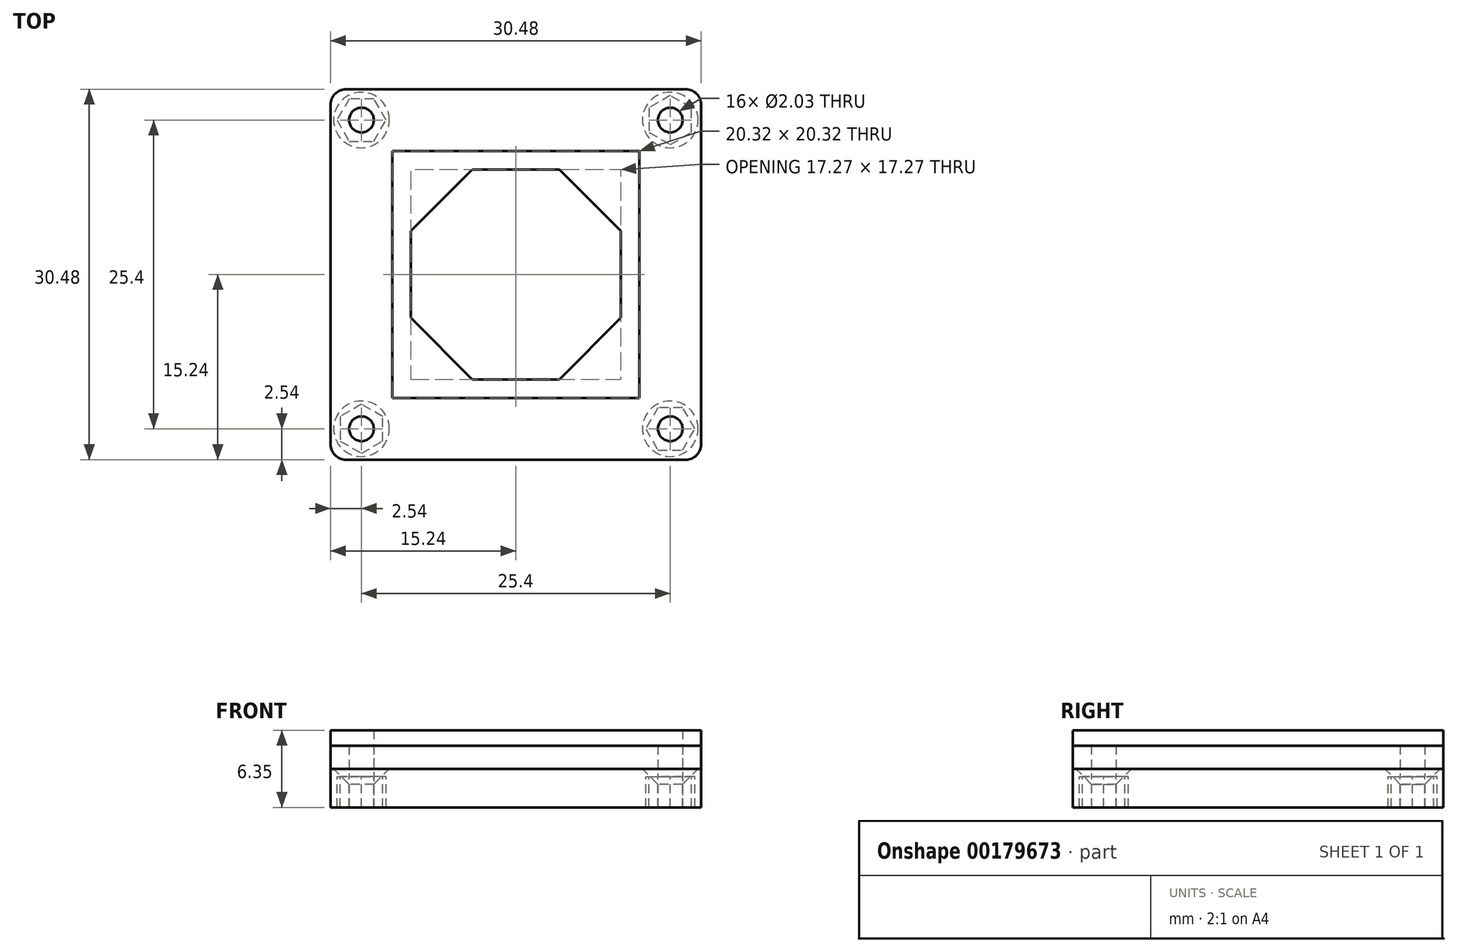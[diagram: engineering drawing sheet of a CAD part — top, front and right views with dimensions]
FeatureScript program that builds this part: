
annotation { "Feature Type Name" : "Feature", "Feature Type Description" : "" }
export const myFeature = defineFeature(function(context is Context, id is Id, definition is map)
    precondition{}
    {
        {
            var Q0;
            Q0=qCreatedBy(makeId("Front.planeOp"),FACE);
            var sketch = newSketch(context, id + "F0", { "sketchPlane" : qUnion([Q0])});
            skLineSegment(sketch, "E0", {"start": v(0, 11.24) * mm, "end": v(0, -12.26) * mm, "construction": true});
            skSolve(sketch);
        }
        {
            var Q0;
            Q0=qCreatedBy(makeId("Top.planeOp"),FACE);
            var sketch = newSketch(context, id + "F1", { "sketchPlane" : qUnion([Q0])});
            skLineSegment(sketch, "E1.bottom", {"start": v(10.16, 10.16) * mm, "end": v(-10.16, 10.16) * mm});
            skLineSegment(sketch, "E1.top", {"start": v(10.16, -10.16) * mm, "end": v(-10.16, -10.16) * mm});
            skLineSegment(sketch, "E1.left", {"start": v(10.16, 10.16) * mm, "end": v(10.16, -10.16) * mm});
            skLineSegment(sketch, "E1.right", {"start": v(-10.16, 10.16) * mm, "end": v(-10.16, -10.16) * mm});
            skPoint(sketch, "E1.middle", {"position": v(0, 0) * mm});
            skCircle(sketch, "E2.cCircle", {"center": v(0, 0) * mm, "radius": 8.64 * mm, "construction": true});
            skPoint(sketch, "E2.cCircle.perimeterSnap0", {"position": v(-10.16, 0) * mm});
            skLineSegment(sketch, "E2.0", {"start": v(-8.64, -3.58) * mm, "end": v(-8.64, 3.58) * mm});
            skLineSegment(sketch, "E2.1", {"start": v(-8.64, 3.58) * mm, "end": v(-3.58, 8.64) * mm});
            skLineSegment(sketch, "E2.2", {"start": v(-3.58, 8.64) * mm, "end": v(3.58, 8.64) * mm});
            skLineSegment(sketch, "E2.3", {"start": v(3.58, 8.64) * mm, "end": v(8.64, 3.58) * mm});
            skLineSegment(sketch, "E2.4", {"start": v(8.64, 3.58) * mm, "end": v(8.64, -3.58) * mm});
            skLineSegment(sketch, "E2.5", {"start": v(8.64, -3.58) * mm, "end": v(3.58, -8.64) * mm});
            skLineSegment(sketch, "E2.6", {"start": v(3.58, -8.64) * mm, "end": v(-3.58, -8.64) * mm});
            skLineSegment(sketch, "E2.7", {"start": v(-3.58, -8.64) * mm, "end": v(-8.64, -3.58) * mm});
            skPoint(sketch, "E2.0.midPoint", {"position": v(-8.64, 0) * mm});
            skPoint(sketch, "E2.0.midPoint.positionSnap0", {"position": v(-10.16, 0) * mm});
            skLineSegment(sketch, "E3.0", {"start": v(-15.24, 15.24) * mm, "end": v(-15.24, -15.24) * mm});
            skLineSegment(sketch, "E3.1", {"start": v(15.24, 15.24) * mm, "end": v(-15.24, 15.24) * mm});
            skLineSegment(sketch, "E3.2", {"start": v(15.24, 15.24) * mm, "end": v(15.24, -15.24) * mm});
            skLineSegment(sketch, "E3.3", {"start": v(15.24, -15.24) * mm, "end": v(-15.24, -15.24) * mm});
            skLineSegment(sketch, "E4", {"start": v(10.16, -10.16) * mm, "end": v(15.24, -15.24) * mm});
            skPoint(sketch, "E5", {"position": v(12.7, -12.7) * mm});
            skCircle(sketch, "E6", {"center": v(12.7, -12.7) * mm, "radius": 1.02 * mm});
            skCircle(sketch, "E7.1.0", {"center": v(12.7, 12.7) * mm, "radius": 1.02 * mm});
            skCircle(sketch, "E7.2.0", {"center": v(-12.7, 12.7) * mm, "radius": 1.02 * mm});
            skCircle(sketch, "E7.3.0", {"center": v(-12.7, -12.7) * mm, "radius": 1.02 * mm});
            skSolve(sketch);
        }
        {
            var Q0;
            Q0=makeQuery(id+"F1.imprint","IMPRINT",FACE,{"disambiguationData":[TD([[makeQuery(id+"F1.imprint","IMPRINT",EDGE,{"derivedFrom":sQuery(id+"F1.wireOp",EDGE,"E1.bottom")}),1.0]])]});
            var Q1;
            Q1=makeQuery(id+"F1.imprint","IMPRINT",FACE,{"disambiguationData":[TD([[makeQuery(id+"F1.imprint","IMPRINT",EDGE,{"derivedFrom":sQuery(id+"F1.wireOp",EDGE,"E1.bottom")}),-1.0]])]});
            extrude(context, id + "F2", {"entities" : qUnion([Q0, Q1]), "depth" : 6.35 * mm});
        }
        {
            var Q0;
            Q0=makeQuery(id+"F2.opExtrude","SWEPT_EDGE",EDGE,{"disambiguationData":[OSD([sQuery(id+"F1.wireOp",EDGE,"E3.0"),sQuery(id+"F1.wireOp",EDGE,"E3.1")])]});
            var Q1;
            Q1=makeQuery(id+"F2.opExtrude","SWEPT_EDGE",EDGE,{"disambiguationData":[OSD([sQuery(id+"F1.wireOp",EDGE,"E3.0"),sQuery(id+"F1.wireOp",EDGE,"E3.3")])]});
            var Q2;
            Q2=makeQuery(id+"F2.opExtrude","SWEPT_EDGE",EDGE,{"disambiguationData":[OSD([sQuery(id+"F1.wireOp",EDGE,"E3.1"),sQuery(id+"F1.wireOp",EDGE,"E3.2")])]});
            var Q3;
            Q3=makeQuery(id+"F2.opExtrude","SWEPT_EDGE",EDGE,{"disambiguationData":[OSD([sQuery(id+"F1.wireOp",EDGE,"E3.2"),sQuery(id+"F1.wireOp",EDGE,"E3.3")])]});
            fillet(context, id + "F3", {"entities" : qUnion([Q0, Q1, Q2, Q3]), "radius" : 1.27 * mm, "tangentPropagation" : true, "allowEdgeOverflow" : false});
        }
        {
            var Q0;
            Q0=makeQuery(id+"F1.imprint","IMPRINT",FACE,{"disambiguationData":[TD([[makeQuery(id+"F1.imprint","IMPRINT",EDGE,{"derivedFrom":sQuery(id+"F1.wireOp",EDGE,"E1.bottom")}),-1.0]])]});
            extrude(context, id + "F4", {"entities" : qUnion([Q0]), "depth" : 6.35 * mm});
        }
        {
            var Q0;
            Q0=makeQuery(id+"F4.opExtrude","SWEPT_EDGE",EDGE,{"disambiguationData":[OSD([sQuery(id+"F1.wireOp",EDGE,"E3.1"),sQuery(id+"F1.wireOp",EDGE,"E3.2")])]});
            var Q1;
            Q1=makeQuery(id+"F4.opExtrude","SWEPT_EDGE",EDGE,{"disambiguationData":[OSD([sQuery(id+"F1.wireOp",EDGE,"E3.2"),sQuery(id+"F1.wireOp",EDGE,"E3.3")])]});
            var Q2;
            Q2=makeQuery(id+"F4.opExtrude","SWEPT_EDGE",EDGE,{"disambiguationData":[OSD([sQuery(id+"F1.wireOp",EDGE,"E3.0"),sQuery(id+"F1.wireOp",EDGE,"E3.1")])]});
            var Q3;
            Q3=makeQuery(id+"F4.opExtrude","SWEPT_EDGE",EDGE,{"disambiguationData":[OSD([sQuery(id+"F1.wireOp",EDGE,"E3.0"),sQuery(id+"F1.wireOp",EDGE,"E3.3")])]});
            fillet(context, id + "F5", {"entities" : qUnion([Q0, Q1, Q2, Q3]), "radius" : 1.27 * mm, "tangentPropagation" : true, "allowEdgeOverflow" : false});
        }
        {
            var Q0;
            Q0=makeQuery(id+"F1.imprint","IMPRINT",FACE,{"disambiguationData":[TD([[makeQuery(id+"F1.imprint","IMPRINT",EDGE,{"derivedFrom":sQuery(id+"F1.wireOp",EDGE,"E1.bottom")}),-1.0]])]});
            var Q1;
            Q1=makeQuery(id+"F1.imprint","IMPRINT",FACE,{"disambiguationData":[TD([[makeQuery(id+"F1.imprint","IMPRINT",EDGE,{"derivedFrom":sQuery(id+"F1.wireOp",EDGE,"E1.bottom")}),1.0]])]});
            var Q2;
            Q2=makeQuery(id+"F1.imprint","IMPRINT",FACE,{"disambiguationData":[TD([[makeQuery(id+"F1.imprint","IMPRINT",EDGE,{"derivedFrom":sQuery(id+"F1.wireOp",EDGE,"E2.0")}),-1.0]])]});
            extrude(context, id + "F6", {"entities" : qUnion([Q0, Q1, Q2]), "depth" : 3.17 * mm});
        }
        {
            var Q0;
            Q0=makeQuery(id+"F6.opExtrude","SWEPT_EDGE",EDGE,{"disambiguationData":[OSD([sQuery(id+"F1.wireOp",EDGE,"E3.0"),sQuery(id+"F1.wireOp",EDGE,"E3.1")])]});
            var Q1;
            Q1=makeQuery(id+"F6.opExtrude","SWEPT_EDGE",EDGE,{"disambiguationData":[OSD([sQuery(id+"F1.wireOp",EDGE,"E3.1"),sQuery(id+"F1.wireOp",EDGE,"E3.2")])]});
            var Q2;
            Q2=makeQuery(id+"F6.opExtrude","SWEPT_EDGE",EDGE,{"disambiguationData":[OSD([sQuery(id+"F1.wireOp",EDGE,"E3.2"),sQuery(id+"F1.wireOp",EDGE,"E3.3")])]});
            var Q3;
            Q3=makeQuery(id+"F6.opExtrude","SWEPT_EDGE",EDGE,{"disambiguationData":[OSD([sQuery(id+"F1.wireOp",EDGE,"E3.0"),sQuery(id+"F1.wireOp",EDGE,"E3.3")])]});
            fillet(context, id + "F7", {"entities" : qUnion([Q0, Q1, Q2, Q3]), "radius" : 1.27 * mm, "tangentPropagation" : true, "allowEdgeOverflow" : false});
        }
        {
            var Q0;
            Q0=makeQuery(id+"F1.imprint","IMPRINT",FACE,{"disambiguationData":[TD([[makeQuery(id+"F1.imprint","IMPRINT",EDGE,{"derivedFrom":sQuery(id+"F1.wireOp",EDGE,"E1.bottom")}),-1.0]])]});
            var Q1;
            Q1=makeQuery(id+"F1.imprint","IMPRINT",FACE,{"disambiguationData":[TD([[makeQuery(id+"F1.imprint","IMPRINT",EDGE,{"derivedFrom":sQuery(id+"F1.wireOp",EDGE,"E1.bottom")}),1.0]])]});
            var Q2;
            Q2=makeQuery(id+"F1.imprint","IMPRINT",FACE,{"disambiguationData":[TD([[makeQuery(id+"F1.imprint","IMPRINT",EDGE,{"derivedFrom":sQuery(id+"F1.wireOp",EDGE,"E2.0")}),-1.0]])]});
            extrude(context, id + "F8", {"entities" : qUnion([Q0, Q1, Q2]), "depth" : 5.08 * mm});
        }
        {
            var Q0;
            Q0=makeQuery(id+"F8.opExtrude","CAP_FACE",FACE,{"disambiguationData":[OSD([sQuery(id+"F1.wireOp",EDGE,"E3.0"),sQuery(id+"F1.wireOp",EDGE,"E3.1"),sQuery(id+"F1.wireOp",EDGE,"E3.2"),sQuery(id+"F1.wireOp",EDGE,"E3.3"),sQuery(id+"F1.wireOp",EDGE,"E6"),sQuery(id+"F1.wireOp",EDGE,"E7.1.0"),sQuery(id+"F1.wireOp",EDGE,"E7.2.0"),sQuery(id+"F1.wireOp",EDGE,"E7.3.0")])],"isStart":true});
            var sketch = newSketch(context, id + "F9", { "sketchPlane" : qUnion([Q0])});
            skCircle(sketch, "E8.cCircle", {"center": v(-12.7, 12.7) * mm, "radius": 1.75 * mm, "construction": true});
            skLineSegment(sketch, "E8.0", {"start": v(-14.45, 11.7) * mm, "end": v(-14.45, 13.7) * mm});
            skLineSegment(sketch, "E8.1", {"start": v(-14.45, 13.7) * mm, "end": v(-12.7, 14.72) * mm});
            skLineSegment(sketch, "E8.2", {"start": v(-12.7, 14.72) * mm, "end": v(-10.95, 13.7) * mm});
            skLineSegment(sketch, "E8.3", {"start": v(-10.95, 13.7) * mm, "end": v(-10.95, 11.7) * mm});
            skLineSegment(sketch, "E8.4", {"start": v(-10.95, 11.7) * mm, "end": v(-12.7, 10.68) * mm});
            skLineSegment(sketch, "E8.5", {"start": v(-12.7, 10.68) * mm, "end": v(-14.45, 11.7) * mm});
            skPoint(sketch, "E8.0.midPoint", {"position": v(-14.45, 12.7) * mm});
            skSolve(sketch);
        }
        {
            var Q0;
            Q0=makeQuery(id+"F9.imprint","IMPRINT",FACE,{"disambiguationData":[TD([[makeQuery(id+"F9.imprint","IMPRINT",EDGE,{"derivedFrom":sQuery(id+"F9.wireOp",EDGE,"E8.0")}),-1.0]])]});
            extrude(context, id + "F10", {"entities" : qUnion([Q0]), "depth" : 5.08 * mm, "symmetric" : true});
        }
        {
            var Q0;
            Q0=makeQuery(id+"F10.opExtrude","SWEPT_BODY",BODY,{"disambiguationData":[OSD([sQuery(id+"F1.wireOp",EDGE,"E7.3.0"),sQuery(id+"F9.wireOp",EDGE,"E8.0"),sQuery(id+"F9.wireOp",EDGE,"E8.1"),sQuery(id+"F9.wireOp",EDGE,"E8.2"),sQuery(id+"F9.wireOp",EDGE,"E8.3"),sQuery(id+"F9.wireOp",EDGE,"E8.4"),sQuery(id+"F9.wireOp",EDGE,"E8.5")])]});
            var Q1;
            Q1=sQuery(id+"F0.wireOp",EDGE,"E0");
            circularPattern(context, id + "F11", {"entities" : qUnion([Q0]), "axis" : qUnion([Q1]), "angle" : 270 * degree, "instanceCount" : 4});
        }
        {
            var Q0;
            Q0=makeQuery(id+"F10.opExtrude","SWEPT_BODY",BODY,{"disambiguationData":[OSD([sQuery(id+"F1.wireOp",EDGE,"E7.3.0"),sQuery(id+"F9.wireOp",EDGE,"E8.0"),sQuery(id+"F9.wireOp",EDGE,"E8.1"),sQuery(id+"F9.wireOp",EDGE,"E8.2"),sQuery(id+"F9.wireOp",EDGE,"E8.3"),sQuery(id+"F9.wireOp",EDGE,"E8.4"),sQuery(id+"F9.wireOp",EDGE,"E8.5")])]});
            var Q1;
            Q1=makeQuery(id+"F11.opPattern","COPY",BODY,{"derivedFrom":makeQuery(id+"F10.opExtrude","SWEPT_BODY",BODY,{"disambiguationData":[OSD([sQuery(id+"F1.wireOp",EDGE,"E7.3.0"),sQuery(id+"F9.wireOp",EDGE,"E8.0"),sQuery(id+"F9.wireOp",EDGE,"E8.1"),sQuery(id+"F9.wireOp",EDGE,"E8.2"),sQuery(id+"F9.wireOp",EDGE,"E8.3"),sQuery(id+"F9.wireOp",EDGE,"E8.4"),sQuery(id+"F9.wireOp",EDGE,"E8.5")])]}),"instanceName":"1"});
            var Q2;
            Q2=makeQuery(id+"F11.opPattern","COPY",BODY,{"derivedFrom":makeQuery(id+"F10.opExtrude","SWEPT_BODY",BODY,{"disambiguationData":[OSD([sQuery(id+"F1.wireOp",EDGE,"E7.3.0"),sQuery(id+"F9.wireOp",EDGE,"E8.0"),sQuery(id+"F9.wireOp",EDGE,"E8.1"),sQuery(id+"F9.wireOp",EDGE,"E8.2"),sQuery(id+"F9.wireOp",EDGE,"E8.3"),sQuery(id+"F9.wireOp",EDGE,"E8.4"),sQuery(id+"F9.wireOp",EDGE,"E8.5")])]}),"instanceName":"2"});
            var Q3;
            Q3=makeQuery(id+"F11.opPattern","COPY",BODY,{"derivedFrom":makeQuery(id+"F10.opExtrude","SWEPT_BODY",BODY,{"disambiguationData":[OSD([sQuery(id+"F1.wireOp",EDGE,"E7.3.0"),sQuery(id+"F9.wireOp",EDGE,"E8.0"),sQuery(id+"F9.wireOp",EDGE,"E8.1"),sQuery(id+"F9.wireOp",EDGE,"E8.2"),sQuery(id+"F9.wireOp",EDGE,"E8.3"),sQuery(id+"F9.wireOp",EDGE,"E8.4"),sQuery(id+"F9.wireOp",EDGE,"E8.5")])]}),"instanceName":"3"});
            var Q4;
            Q4=makeQuery(id+"F8.opExtrude","SWEPT_BODY",BODY,{"disambiguationData":[OSD([sQuery(id+"F1.wireOp",EDGE,"E3.0"),sQuery(id+"F1.wireOp",EDGE,"E3.1"),sQuery(id+"F1.wireOp",EDGE,"E3.2"),sQuery(id+"F1.wireOp",EDGE,"E3.3"),sQuery(id+"F1.wireOp",EDGE,"E6"),sQuery(id+"F1.wireOp",EDGE,"E7.1.0"),sQuery(id+"F1.wireOp",EDGE,"E7.2.0"),sQuery(id+"F1.wireOp",EDGE,"E7.3.0")])]});
            booleanBodies(context, id + "F12", {"operationType" : BooleanOperationType.SUBTRACTION, "tools" : qUnion([Q0, Q1, Q2, Q3]), "targets" : qUnion([Q4])});
        }
        {
            var Q0;
            Q0=makeQuery(id+"F8.opExtrude","SWEPT_EDGE",EDGE,{"disambiguationData":[OSD([sQuery(id+"F1.wireOp",EDGE,"E3.2"),sQuery(id+"F1.wireOp",EDGE,"E3.3")])]});
            var Q1;
            Q1=makeQuery(id+"F8.opExtrude","SWEPT_EDGE",EDGE,{"disambiguationData":[OSD([sQuery(id+"F1.wireOp",EDGE,"E3.0"),sQuery(id+"F1.wireOp",EDGE,"E3.3")])]});
            var Q2;
            Q2=makeQuery(id+"F8.opExtrude","SWEPT_EDGE",EDGE,{"disambiguationData":[OSD([sQuery(id+"F1.wireOp",EDGE,"E3.0"),sQuery(id+"F1.wireOp",EDGE,"E3.1")])]});
            var Q3;
            Q3=makeQuery(id+"F8.opExtrude","SWEPT_EDGE",EDGE,{"disambiguationData":[OSD([sQuery(id+"F1.wireOp",EDGE,"E3.1"),sQuery(id+"F1.wireOp",EDGE,"E3.2")])]});
            fillet(context, id + "F13", {"entities" : qUnion([Q0, Q1, Q2, Q3]), "radius" : 1.27 * mm, "tangentPropagation" : true, "allowEdgeOverflow" : false});
        }
        {
            var Q0;
            Q0=makeQuery(id+"F6.opExtrude","CAP_EDGE",EDGE,{"disambiguationData":[OSD([sQuery(id+"F1.wireOp",EDGE,"E7.3.0")])],"isStart":false});
            var Q1;
            Q1=makeQuery(id+"F6.opExtrude","CAP_EDGE",EDGE,{"disambiguationData":[OSD([sQuery(id+"F1.wireOp",EDGE,"E7.2.0")])],"isStart":false});
            var Q2;
            Q2=makeQuery(id+"F6.opExtrude","CAP_EDGE",EDGE,{"disambiguationData":[OSD([sQuery(id+"F1.wireOp",EDGE,"E7.1.0")])],"isStart":false});
            var Q3;
            Q3=makeQuery(id+"F6.opExtrude","CAP_EDGE",EDGE,{"disambiguationData":[OSD([sQuery(id+"F1.wireOp",EDGE,"E6")])],"isStart":false});
            chamfer(context, id + "F14", {"entities" : qUnion([Q0, Q1, Q2, Q3]), "width" : 1.27 * mm, "tangentPropagation" : true});
        }
    });
